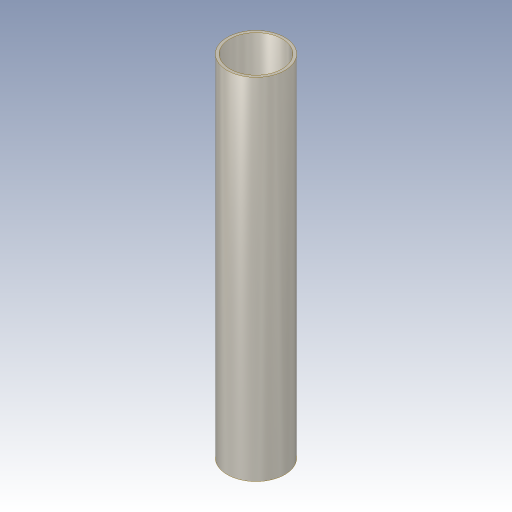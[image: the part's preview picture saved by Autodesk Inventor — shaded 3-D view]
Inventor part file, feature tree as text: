
AUTODESK INVENTOR PART (.ipt)
format: ipt  version: 2023.3 (Build 273359000, 359)  size: 128,512 bytes
history: native  units: in
note: dims shown in document units (in); Inventor stores cm internally (conversion verified against a paired STEP export)
features: revolve x1, sketch x1
ambient origin geometry x8: Origin, YZ Plane, XZ Plane, XY Plane, X Axis, Y Axis, Z Axis, Center Point
bodies: Body1 (feature_tree)
feature tree (2):
  revolve  "Umdrehung1"
  sketch  "Skizze3"  dims[d4=0.0937in d5=0.5709in d6=0.085in d7=90.0deg]
